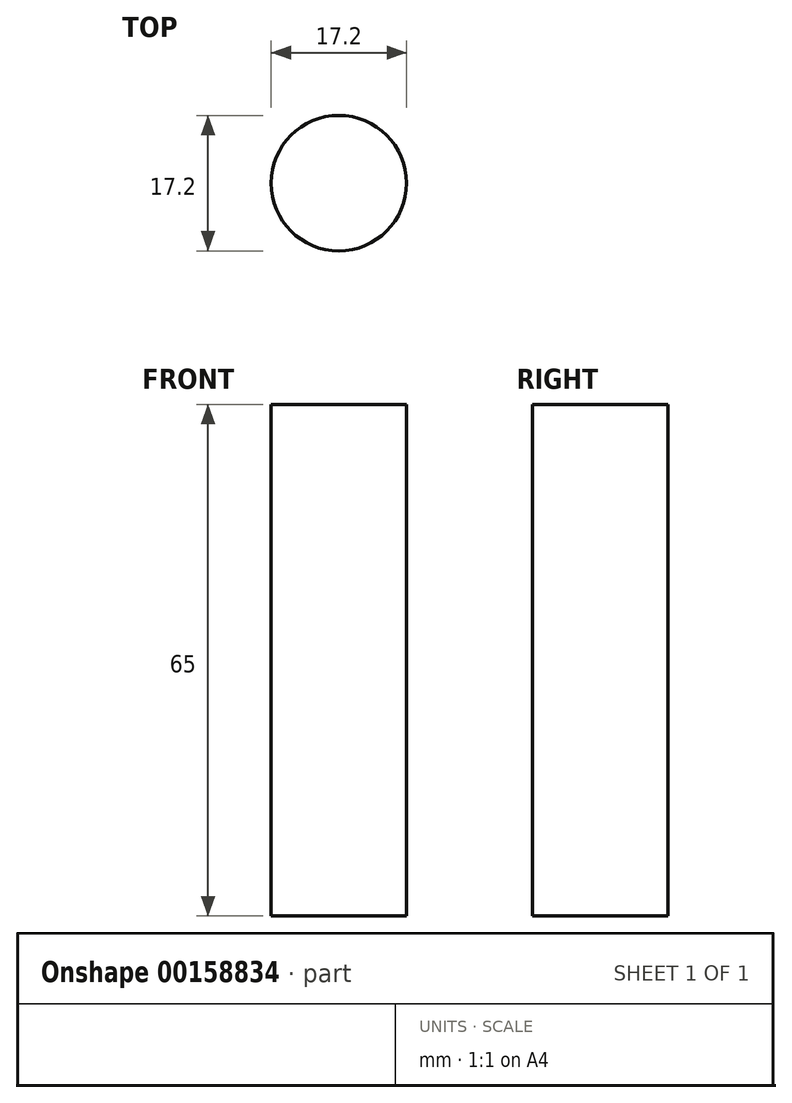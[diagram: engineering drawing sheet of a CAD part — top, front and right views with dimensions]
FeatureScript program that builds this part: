
annotation { "Feature Type Name" : "Feature", "Feature Type Description" : "" }
export const myFeature = defineFeature(function(context is Context, id is Id, definition is map)
    precondition{}
    {
        {
            var Q0;
            Q0=qCreatedBy(makeId("Top.planeOp"),FACE);
            var sketch = newSketch(context, id + "F0", { "sketchPlane" : qUnion([Q0])});
            skCircle(sketch, "E0", {"center": v(0, 0) * mm, "radius": 8.6 * mm});
            skSolve(sketch);
        }
        {
            var Q0;
            Q0 = qSketchRegion(id + "F0", true);
            extrude(context, id + "F1", {"entities" : qUnion([Q0]), "depth" : 65 * mm});
        }
    });
